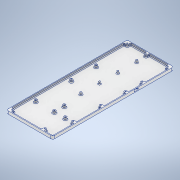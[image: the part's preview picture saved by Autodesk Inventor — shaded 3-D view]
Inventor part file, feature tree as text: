
AUTODESK INVENTOR PART (.ipt)
format: ipt  version: 2022 (Build 260153000, 153)  size: 563,712 bytes
history: native  units: mm
features: sketch x24, hole x15, extrude x7, fillet x4, other x2
ambient origin geometry x8: Origin, YZ Plane, XZ Plane, XY Plane, X Axis, Y Axis, Z Axis, Center Point
bodies: Body1 (feature_tree)
feature tree (52):
  other  "作業平面5"
  extrude  "押し出し12"  Depth=142.24mm
  extrude  "押し出し13"  Depth=371.475mm
  extrude  "押し出し14"  Depth=6.0mm
  extrude  "押し出し15"  Depth=2.6mm TaperAngle=0.0deg
  extrude  "押し出し16"  Depth=6.0mm
  fillet  "フィレット8"  Radius=2.54mm
  sketch  "スケッチ23"
  extrude  "押し出し17"  Depth=6.4mm TaperAngle=0.0deg
  sketch  "スケッチ28"
  sketch  "スケッチ32"
  sketch  "スケッチ33"
  sketch  "スケッチ34"
  sketch  "スケッチ35"
  sketch  "スケッチ36"
  sketch  "スケッチ37"
  sketch  "スケッチ38"
  sketch  "スケッチ39"
  sketch  "スケッチ40"
  sketch  "スケッチ41"
  sketch  "スケッチ42"
  sketch  "スケッチ43"
  sketch  "スケッチ44"
  sketch  "スケッチ45"
  sketch  "スケッチ46"
  sketch  "スケッチ47"
  hole  "穴1"  [1 undecoded]
  hole  "穴2"  [1 undecoded]
  hole  "穴3"  [1 undecoded]
  hole  "穴4"  [1 undecoded]
  hole  "穴5"  [1 undecoded]
  hole  "穴6"  [1 undecoded]
  hole  "穴7"  [1 undecoded]
  hole  "穴8"  [1 undecoded]
  hole  "穴9"  [1 undecoded]
  hole  "穴10"  [1 undecoded]
  hole  "穴11"  [1 undecoded]
  hole  "穴12"  [1 undecoded]
  hole  "穴13"  [1 undecoded]
  hole  "穴14"  [1 undecoded]
  hole  "穴15"  [1 undecoded]
  fillet  "フィレット13"  Radius=56.39mm
  fillet  "フィレット14"  Radius=57.4mm
  extrude  "押し出し18"  Depth=6.4mm TaperAngle=0.0deg
  fillet  "フィレット15"  Radius=2.0mm
  sketch  "スケッチ16"
  other  "ソリッド2"
  sketch  "スケッチ17"
  sketch  "スケッチ18"
  sketch  "スケッチ21"
  sketch  "スケッチ24"
  sketch  "スケッチ48"
note: 15 required parameter values undecoded (feature->parameter linkage not recoverable at this tier; creation-order binding heuristic only, values carry confidence <= 0.55)
